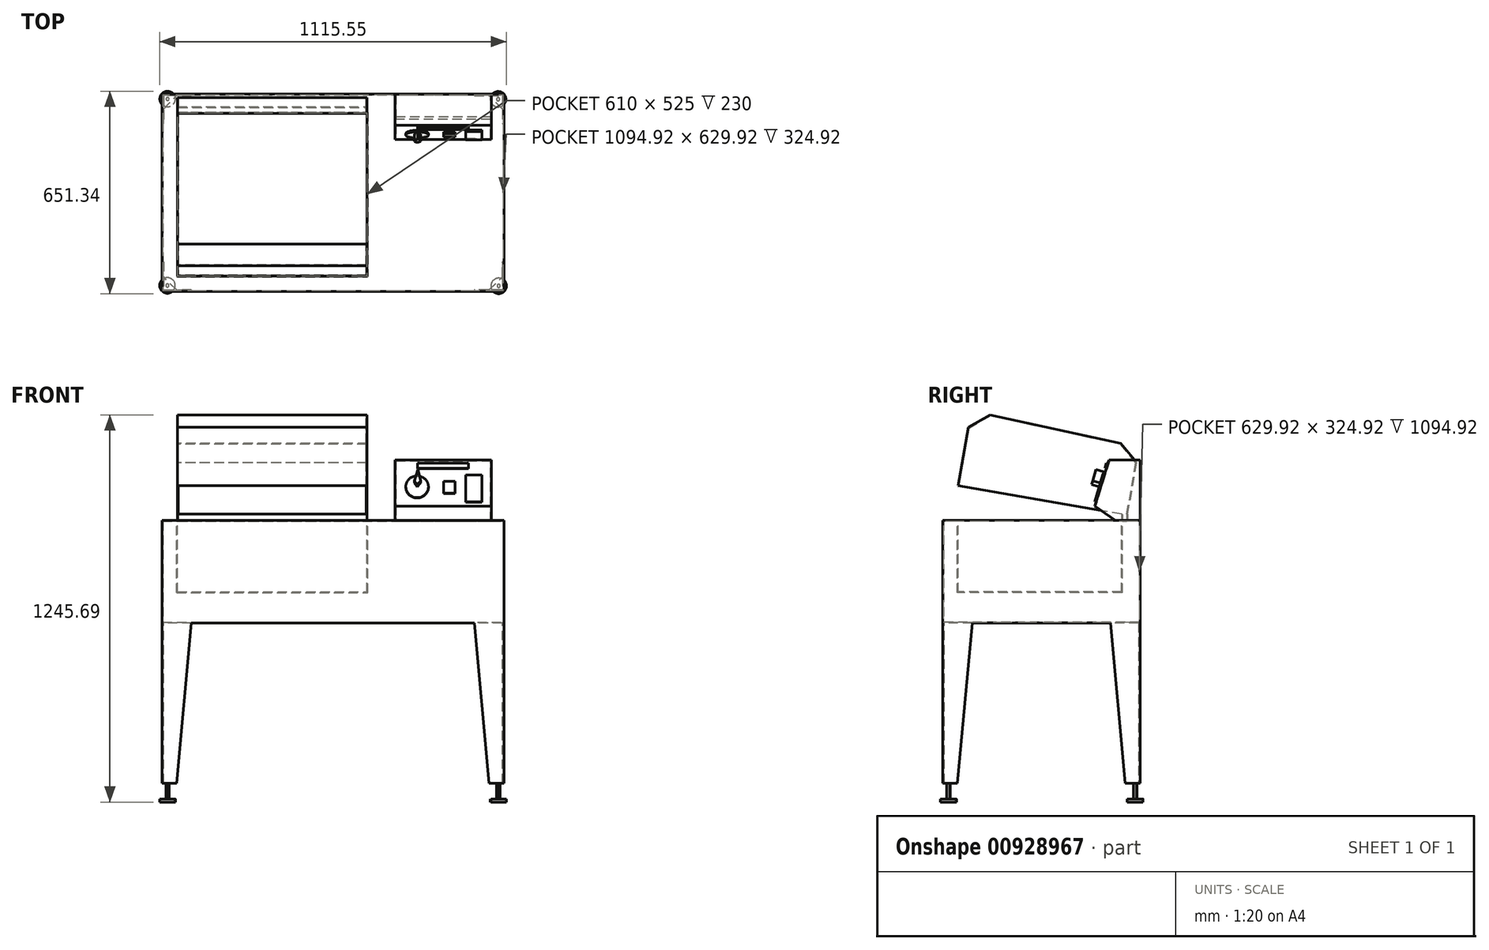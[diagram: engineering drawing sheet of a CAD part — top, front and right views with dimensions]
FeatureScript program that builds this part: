
annotation { "Feature Type Name" : "Feature", "Feature Type Description" : "" }
export const myFeature = defineFeature(function(context is Context, id is Id, definition is map)
    precondition{}
    {
        {
            var Q0;
            Q0=qCreatedBy(makeId("Front.planeOp"),FACE);
            var sketch = newSketch(context, id + "F0", { "sketchPlane" : qUnion([Q0])});
            skLineSegment(sketch, "E0", {"start": v(0, 749.43) * mm, "end": v(0, -565.58) * mm, "construction": true});
            skLineSegment(sketch, "E1", {"start": v(-789.94, 0) * mm, "end": v(708.92, 0) * mm, "construction": true});
            skLineSegment(sketch, "E2.bottom", {"start": v(-550, 165) * mm, "end": v(550, 165) * mm});
            skLineSegment(sketch, "E2.top", {"start": v(-550, -165) * mm, "end": v(550, -165) * mm});
            skLineSegment(sketch, "E2.left", {"start": v(-550, 165) * mm, "end": v(-550, -165) * mm});
            skLineSegment(sketch, "E2.right", {"start": v(550, 165) * mm, "end": v(550, -165) * mm});
            skSolve(sketch);
        }
        {
            var Q0;
            Q0 = qSketchRegion(id + "F0", true);
            extrude(context, id + "F1", {"entities" : qUnion([Q0]), "oppositeDirection" : true, "depth" : 635 * mm, "offsetDistance" : 25.4 * mm});
        }
        {
            var Q0;
            Q0=makeQuery(id+"F1.opExtrude","SWEPT_FACE",FACE,{"disambiguationData":[OSD([sQuery(id+"F0.wireOp",EDGE,"E2.bottom")])]});
            var sketch = newSketch(context, id + "F2", { "sketchPlane" : qUnion([Q0])});
            skLineSegment(sketch, "E3.bottom", {"start": v(510, 635) * mm, "end": v(200, 635) * mm});
            skLineSegment(sketch, "E3.top", {"start": v(510, 465) * mm, "end": v(200, 465) * mm});
            skLineSegment(sketch, "E3.left", {"start": v(510, 635) * mm, "end": v(510, 465) * mm});
            skLineSegment(sketch, "E3.right", {"start": v(200, 635) * mm, "end": v(200, 465) * mm});
            skSolve(sketch);
        }
        {
            var Q0;
            Q0 = qSketchRegion(id + "F2", true);
            extrude(context, id + "F3", {"entities" : qUnion([Q0]), "operationType" : NewBodyOperationType.ADD, "depth" : 195 * mm, "offsetDistance" : 25.4 * mm});
        }
        {
            var Q0;
            Q0=makeQuery(id+"F3.opExtrude","SWEPT_FACE",FACE,{"disambiguationData":[OSD([sQuery(id+"F2.wireOp",EDGE,"E3.left")])]});
            var sketch = newSketch(context, id + "F4", { "sketchPlane" : qUnion([Q0])});
            skLineSegment(sketch, "E4", {"start": v(635, 360) * mm, "end": v(535, 360) * mm});
            skLineSegment(sketch, "E5", {"start": v(635, 165) * mm, "end": v(555, 165) * mm});
            skLineSegment(sketch, "E6", {"start": v(555, 165) * mm, "end": v(489.35, 210.72) * mm});
            skLineSegment(sketch, "E7", {"start": v(489.35, 210.72) * mm, "end": v(535, 360) * mm});
            skLineSegment(sketch, "E8", {"start": v(555, 165) * mm, "end": v(465, 165) * mm});
            skLineSegment(sketch, "E9", {"start": v(465, 165) * mm, "end": v(465, 360) * mm});
            skLineSegment(sketch, "E10", {"start": v(465, 360) * mm, "end": v(535, 360) * mm});
            skSolve(sketch);
        }
        {
            var Q0;
            Q0=makeQuery(id+"F4.imprint","IMPRINT",FACE,{"disambiguationData":[TD([[makeQuery(id+"F4.imprint","IMPRINT",EDGE,{"derivedFrom":sQuery(id+"F4.wireOp",EDGE,"E6")}),1.0]])]});
            extrude(context, id + "F5", {"entities" : qUnion([Q0]), "operationType" : NewBodyOperationType.REMOVE, "endBound" : BoundingType.UP_TO_NEXT, "oppositeDirection" : true, "depth" : 25.4 * mm, "offsetDistance" : 25.4 * mm});
        }
        {
            var Q0;
            Q0=makeQuery(id+"F5.boolean.opBoolean","MERGE",FACE,{"derivedFrom":[makeQuery(id+"F1.opExtrude","SWEPT_FACE",FACE,{"disambiguationData":[OSD([sQuery(id+"F0.wireOp",EDGE,"E2.bottom")])]})],"fromTools":[makeQuery(id+"F5.opExtrude","SWEPT_FACE",FACE,{"disambiguationData":[OSD([sQuery(id+"F4.wireOp",EDGE,"E8")])]})]});
            var sketch = newSketch(context, id + "F6", { "sketchPlane" : qUnion([Q0])});
            skLineSegment(sketch, "E11.bottom", {"start": v(-500, 575) * mm, "end": v(110, 575) * mm});
            skLineSegment(sketch, "E11.top", {"start": v(-500, 50) * mm, "end": v(110, 50) * mm});
            skLineSegment(sketch, "E11.left", {"start": v(-500, 575) * mm, "end": v(-500, 50) * mm});
            skLineSegment(sketch, "E11.right", {"start": v(110, 575) * mm, "end": v(110, 50) * mm});
            skSolve(sketch);
        }
        {
            var Q0;
            Q0 = qSketchRegion(id + "F6", true);
            extrude(context, id + "F7", {"entities" : qUnion([Q0]), "operationType" : NewBodyOperationType.REMOVE, "oppositeDirection" : true, "depth" : 230 * mm, "offsetDistance" : 25.4 * mm});
        }
        {
            var Q0;
            Q0=makeQuery(id+"F5.boolean.opBoolean","MERGE",FACE,{"derivedFrom":[makeQuery(id+"F1.opExtrude","SWEPT_FACE",FACE,{"disambiguationData":[OSD([sQuery(id+"F0.wireOp",EDGE,"E2.bottom")])]})],"fromTools":[makeQuery(id+"F5.opExtrude","SWEPT_FACE",FACE,{"disambiguationData":[OSD([sQuery(id+"F4.wireOp",EDGE,"E8")])]})]});
            var sketch = newSketch(context, id + "F8", { "sketchPlane" : qUnion([Q0])});
            skLineSegment(sketch, "E12.bottom", {"start": v(-500, 575) * mm, "end": v(110, 575) * mm});
            skLineSegment(sketch, "E12.top", {"start": v(-500, 595) * mm, "end": v(110, 595) * mm});
            skLineSegment(sketch, "E12.left", {"start": v(-500, 575) * mm, "end": v(-500, 595) * mm});
            skLineSegment(sketch, "E12.right", {"start": v(110, 575) * mm, "end": v(110, 595) * mm});
            skSolve(sketch);
        }
        {
            var Q0;
            Q0 = qSketchRegion(id + "F8", true);
            extrude(context, id + "F9", {"entities" : qUnion([Q0]), "operationType" : NewBodyOperationType.ADD, "depth" : 20 * mm, "offsetDistance" : 25.4 * mm});
        }
        {
            var Q0;
            Q0=makeQuery(id+"F9.opExtrude","SWEPT_FACE",FACE,{"disambiguationData":[OSD([sQuery(id+"F8.wireOp",EDGE,"E12.left")])]});
            var sketch = newSketch(context, id + "F10", { "sketchPlane" : qUnion([Q0])});
            skLineSegment(sketch, "E13", {"start": v(-575, 185) * mm, "end": v(-50, 277.57) * mm});
            skLineSegment(sketch, "E14", {"start": v(-50, 277.57) * mm, "end": v(-83, 464.69) * mm});
            skLineSegment(sketch, "E15", {"start": v(-595, 185) * mm, "end": v(-624.3, 351.17) * mm});
            skLineSegment(sketch, "E16", {"start": v(-624.3, 351.17) * mm, "end": v(-572.88, 412.45) * mm});
            skLineSegment(sketch, "E17", {"start": v(-83, 464.69) * mm, "end": v(-152.28, 504.69) * mm});
            skLineSegment(sketch, "E18", {"start": v(-572.88, 412.45) * mm, "end": v(-152.28, 504.69) * mm});
            skLineSegment(sketch, "E19", {"start": v(-595, 185) * mm, "end": v(-575, 185) * mm});
            skSolve(sketch);
        }
        {
            var Q0;
            Q0 = qSketchRegion(id + "F10", true);
            var Q1;
            Q1=makeQuery(id+"F9.opExtrude","CAP_VERTEX",VERTEX,{"disambiguationData":[OSD([sQuery(id+"F6.wireOp",EDGE,"E11.right"),sQuery(id+"F8.wireOp",EDGE,"E12.bottom"),sQuery(id+"F8.wireOp",EDGE,"E12.right")])],"isStart":false});
            extrude(context, id + "F11", {"entities" : qUnion([Q0]), "operationType" : NewBodyOperationType.ADD, "endBound" : BoundingType.UP_TO_VERTEX, "oppositeDirection" : true, "depth" : 25.4 * mm, "endBoundEntityVertex" : qUnion([Q1]), "offsetDistance" : 25.4 * mm});
        }
        {
            var Q0;
            Q0=makeQuery(id+"F11.opExtrude","SWEPT_FACE",FACE,{"disambiguationData":[OSD([sQuery(id+"F10.wireOp",EDGE,"E13")])]});
            shell(context, id + "F12", {"entities" : qUnion([Q0]), "thickness" : 2.54 * mm});
        }
        {
            var Q0;
            Q0=makeQuery(id+"F1.opExtrude","SWEPT_FACE",FACE,{"disambiguationData":[OSD([sQuery(id+"F0.wireOp",EDGE,"E2.top")])]});
            var sketch = newSketch(context, id + "F13", { "sketchPlane" : qUnion([Q0])});
            skLineSegment(sketch, "E20", {"start": v(-455, 0) * mm, "end": v(-550, 0) * mm});
            skLineSegment(sketch, "E21", {"start": v(-550, 0) * mm, "end": v(-550, -95) * mm});
            skLineSegment(sketch, "E22", {"start": v(-550, -95) * mm, "end": v(-545, -95) * mm});
            skLineSegment(sketch, "E23", {"start": v(-545, -95) * mm, "end": v(-545, -5) * mm});
            skLineSegment(sketch, "E24", {"start": v(-545, -5) * mm, "end": v(-455, -5) * mm});
            skLineSegment(sketch, "E25", {"start": v(-455, -5) * mm, "end": v(-455, 0) * mm});
            skLineSegment(sketch, "E26", {"start": v(455, 0) * mm, "end": v(550, 0) * mm});
            skLineSegment(sketch, "E27", {"start": v(550, 0) * mm, "end": v(550, -95) * mm});
            skLineSegment(sketch, "E28", {"start": v(550, -95) * mm, "end": v(545, -95) * mm});
            skLineSegment(sketch, "E29", {"start": v(545, -95) * mm, "end": v(545, -5) * mm});
            skLineSegment(sketch, "E30", {"start": v(545, -5) * mm, "end": v(455, -5) * mm});
            skLineSegment(sketch, "E31", {"start": v(455, -5) * mm, "end": v(455, 0) * mm});
            skLineSegment(sketch, "E32", {"start": v(-550, -540) * mm, "end": v(-550, -635) * mm});
            skLineSegment(sketch, "E33", {"start": v(-550, -635) * mm, "end": v(-455, -635) * mm});
            skLineSegment(sketch, "E34", {"start": v(-455, -635) * mm, "end": v(-455, -630) * mm});
            skLineSegment(sketch, "E35", {"start": v(-455, -630) * mm, "end": v(-545, -630) * mm});
            skLineSegment(sketch, "E36", {"start": v(-545, -630) * mm, "end": v(-545, -540) * mm});
            skLineSegment(sketch, "E37", {"start": v(-545, -540) * mm, "end": v(-550, -540) * mm});
            skLineSegment(sketch, "E38", {"start": v(550, -540) * mm, "end": v(550, -635) * mm});
            skLineSegment(sketch, "E39", {"start": v(550, -635) * mm, "end": v(455, -635) * mm});
            skLineSegment(sketch, "E40", {"start": v(455, -635) * mm, "end": v(455, -630) * mm});
            skLineSegment(sketch, "E41", {"start": v(455, -630) * mm, "end": v(545, -630) * mm});
            skLineSegment(sketch, "E42", {"start": v(545, -630) * mm, "end": v(545, -540) * mm});
            skLineSegment(sketch, "E43", {"start": v(545, -540) * mm, "end": v(550, -540) * mm});
            skSolve(sketch);
        }
        {
            var Q0;
            Q0 = qSketchRegion(id + "F13", true);
            extrude(context, id + "F14", {"entities" : qUnion([Q0]), "operationType" : NewBodyOperationType.ADD, "depth" : 515 * mm, "offsetDistance" : 25.4 * mm});
        }
        {
            var Q0;
            Q0=makeQuery(id+"F14.boolean.opBoolean","MERGE",FACE,{"derivedFrom":[makeQuery(id+"F1.opExtrude","CAP_FACE",FACE,{"disambiguationData":[OSD([sQuery(id+"F0.wireOp",EDGE,"E2.bottom"),sQuery(id+"F0.wireOp",EDGE,"E2.top"),sQuery(id+"F0.wireOp",EDGE,"E2.left"),sQuery(id+"F0.wireOp",EDGE,"E2.right")])],"isStart":true}),makeQuery(id+"F14.opExtrude","SWEPT_FACE",FACE,{"disambiguationData":[OSD([sQuery(id+"F13.wireOp",EDGE,"E20")])]})]});
            var sketch = newSketch(context, id + "F15", { "sketchPlane" : qUnion([Q0])});
            skLineSegment(sketch, "E44", {"start": v(-455, -165) * mm, "end": v(-502.5, -680) * mm});
            skLineSegment(sketch, "E45", {"start": v(-502.5, -680) * mm, "end": v(-455, -680) * mm});
            skLineSegment(sketch, "E46", {"start": v(-455, -680) * mm, "end": v(-455, -165) * mm});
            skSolve(sketch);
        }
        {
            var Q0;
            Q0 = qSketchRegion(id + "F15", true);
            extrude(context, id + "F16", {"entities" : qUnion([Q0]), "operationType" : NewBodyOperationType.REMOVE, "oppositeDirection" : true, "depth" : 25.4 * mm, "offsetDistance" : 25.4 * mm});
        }
        {
            var Q0;
            Q0=makeQuery(id+"F14.boolean.opBoolean","MERGE",FACE,{"derivedFrom":[makeQuery(id+"F1.opExtrude","SWEPT_FACE",FACE,{"disambiguationData":[OSD([sQuery(id+"F0.wireOp",EDGE,"E2.left")])]}),makeQuery(id+"F14.opExtrude","SWEPT_FACE",FACE,{"disambiguationData":[OSD([sQuery(id+"F13.wireOp",EDGE,"E21")])]})]});
            var sketch = newSketch(context, id + "F17", { "sketchPlane" : qUnion([Q0])});
            skLineSegment(sketch, "E47", {"start": v(-95, -165) * mm, "end": v(-47.5, -680) * mm});
            skLineSegment(sketch, "E48", {"start": v(-47.5, -680) * mm, "end": v(-95, -680) * mm});
            skLineSegment(sketch, "E49", {"start": v(-95, -680) * mm, "end": v(-95, -165) * mm});
            skSolve(sketch);
        }
        {
            var Q0;
            Q0 = qSketchRegion(id + "F17", true);
            extrude(context, id + "F18", {"entities" : qUnion([Q0]), "operationType" : NewBodyOperationType.REMOVE, "oppositeDirection" : true, "depth" : 25.4 * mm, "offsetDistance" : 25.4 * mm});
        }
        {
            var Q0;
            Q0=makeQuery(id+"F14.boolean.opBoolean","MERGE",FACE,{"derivedFrom":[makeQuery(id+"F1.opExtrude","CAP_FACE",FACE,{"disambiguationData":[OSD([sQuery(id+"F0.wireOp",EDGE,"E2.bottom"),sQuery(id+"F0.wireOp",EDGE,"E2.top"),sQuery(id+"F0.wireOp",EDGE,"E2.left"),sQuery(id+"F0.wireOp",EDGE,"E2.right")])],"isStart":true}),makeQuery(id+"F14.opExtrude","SWEPT_FACE",FACE,{"disambiguationData":[OSD([sQuery(id+"F13.wireOp",EDGE,"E20")])]}),makeQuery(id+"F14.opExtrude","SWEPT_FACE",FACE,{"disambiguationData":[OSD([sQuery(id+"F13.wireOp",EDGE,"E26")])]})]});
            var sketch = newSketch(context, id + "F19", { "sketchPlane" : qUnion([Q0])});
            skLineSegment(sketch, "E50", {"start": v(455, -165) * mm, "end": v(502.5, -680) * mm});
            skLineSegment(sketch, "E51", {"start": v(502.5, -680) * mm, "end": v(455, -680) * mm});
            skLineSegment(sketch, "E52", {"start": v(455, -680) * mm, "end": v(455, -165) * mm});
            skSolve(sketch);
        }
        {
            var Q0;
            Q0 = qSketchRegion(id + "F19", true);
            extrude(context, id + "F20", {"entities" : qUnion([Q0]), "operationType" : NewBodyOperationType.REMOVE, "oppositeDirection" : true, "depth" : 840.74 * mm, "offsetDistance" : 25.4 * mm});
        }
        {
            var Q0;
            Q0=makeQuery(id+"F14.boolean.opBoolean","MERGE",FACE,{"derivedFrom":[makeQuery(id+"F1.opExtrude","SWEPT_FACE",FACE,{"disambiguationData":[OSD([sQuery(id+"F0.wireOp",EDGE,"E2.right")])]}),makeQuery(id+"F14.opExtrude","SWEPT_FACE",FACE,{"disambiguationData":[OSD([sQuery(id+"F13.wireOp",EDGE,"E27")])]}),makeQuery(id+"F14.opExtrude","SWEPT_FACE",FACE,{"disambiguationData":[OSD([sQuery(id+"F13.wireOp",EDGE,"E38")])]})]});
            var sketch = newSketch(context, id + "F21", { "sketchPlane" : qUnion([Q0])});
            skLineSegment(sketch, "E53", {"start": v(95, -165) * mm, "end": v(47.5, -680) * mm});
            skLineSegment(sketch, "E54", {"start": v(47.5, -680) * mm, "end": v(95, -680) * mm});
            skLineSegment(sketch, "E55", {"start": v(95, -680) * mm, "end": v(95, -165) * mm});
            skLineSegment(sketch, "E56", {"start": v(540, -165) * mm, "end": v(587.5, -680) * mm});
            skLineSegment(sketch, "E57", {"start": v(587.5, -680) * mm, "end": v(540, -680) * mm});
            skLineSegment(sketch, "E58", {"start": v(540, -680) * mm, "end": v(540, -165) * mm});
            skSolve(sketch);
        }
        {
            var Q0;
            Q0 = qSketchRegion(id + "F21", true);
            extrude(context, id + "F22", {"entities" : qUnion([Q0]), "operationType" : NewBodyOperationType.REMOVE, "oppositeDirection" : true, "depth" : 25.4 * mm, "offsetDistance" : 25.4 * mm});
        }
        {
            var Q0;
            Q0=makeQuery(id+"F14.boolean.opBoolean","MERGE",FACE,{"derivedFrom":[makeQuery(id+"F3.boolean.opBoolean","MERGE",FACE,{"derivedFrom":[makeQuery(id+"F1.opExtrude","CAP_FACE",FACE,{"disambiguationData":[OSD([sQuery(id+"F0.wireOp",EDGE,"E2.bottom"),sQuery(id+"F0.wireOp",EDGE,"E2.top"),sQuery(id+"F0.wireOp",EDGE,"E2.left"),sQuery(id+"F0.wireOp",EDGE,"E2.right")])],"isStart":false}),makeQuery(id+"F3.opExtrude","SWEPT_FACE",FACE,{"disambiguationData":[OSD([sQuery(id+"F2.wireOp",EDGE,"E3.bottom")])]})]}),makeQuery(id+"F14.opExtrude","SWEPT_FACE",FACE,{"disambiguationData":[OSD([sQuery(id+"F13.wireOp",EDGE,"E33")])]}),makeQuery(id+"F14.opExtrude","SWEPT_FACE",FACE,{"disambiguationData":[OSD([sQuery(id+"F13.wireOp",EDGE,"E39")])]})]});
            var sketch = newSketch(context, id + "F23", { "sketchPlane" : qUnion([Q0])});
            skLineSegment(sketch, "E59", {"start": v(455, -165) * mm, "end": v(502.5, -680) * mm});
            skLineSegment(sketch, "E60", {"start": v(502.5, -680) * mm, "end": v(455, -680) * mm});
            skLineSegment(sketch, "E61", {"start": v(455, -680) * mm, "end": v(455, -165) * mm});
            skSolve(sketch);
        }
        {
            var Q0;
            Q0 = qSketchRegion(id + "F23", true);
            extrude(context, id + "F24", {"entities" : qUnion([Q0]), "operationType" : NewBodyOperationType.REMOVE, "oppositeDirection" : true, "depth" : 25.4 * mm, "offsetDistance" : 25.4 * mm});
        }
        {
            var Q0;
            Q0=makeQuery(id+"F14.boolean.opBoolean","MERGE",FACE,{"derivedFrom":[makeQuery(id+"F1.opExtrude","SWEPT_FACE",FACE,{"disambiguationData":[OSD([sQuery(id+"F0.wireOp",EDGE,"E2.left")])]}),makeQuery(id+"F14.opExtrude","SWEPT_FACE",FACE,{"disambiguationData":[OSD([sQuery(id+"F13.wireOp",EDGE,"E21")])]}),makeQuery(id+"F14.opExtrude","SWEPT_FACE",FACE,{"disambiguationData":[OSD([sQuery(id+"F13.wireOp",EDGE,"E32")])]})]});
            var sketch = newSketch(context, id + "F25", { "sketchPlane" : qUnion([Q0])});
            skLineSegment(sketch, "E62", {"start": v(-540, -165) * mm, "end": v(-587.5, -680) * mm});
            skLineSegment(sketch, "E63", {"start": v(-587.5, -680) * mm, "end": v(-540, -680) * mm});
            skLineSegment(sketch, "E64", {"start": v(-540, -680) * mm, "end": v(-540, -165) * mm});
            skSolve(sketch);
        }
        {
            var Q0;
            Q0 = qSketchRegion(id + "F25", true);
            extrude(context, id + "F26", {"entities" : qUnion([Q0]), "operationType" : NewBodyOperationType.REMOVE, "oppositeDirection" : true, "depth" : 25.4 * mm, "offsetDistance" : 25.4 * mm});
        }
        {
            var Q0;
            Q0=makeQuery(id+"F5.boolean.opBoolean","COPY",FACE,{"derivedFrom":makeQuery(id+"F5.opExtrude","SWEPT_FACE",FACE,{"disambiguationData":[OSD([sQuery(id+"F4.wireOp",EDGE,"E7")])]})});
            var sketch = newSketch(context, id + "F27", { "sketchPlane" : qUnion([Q0])});
            skCircle(sketch, "E65", {"center": v(270.73, 408.7) * mm, "radius": 36.44 * mm});
            skLineSegment(sketch, "E66.bottom", {"start": v(272.44, 488.09) * mm, "end": v(435.25, 488.09) * mm});
            skLineSegment(sketch, "E66.top", {"start": v(272.44, 471.45) * mm, "end": v(435.25, 471.45) * mm});
            skLineSegment(sketch, "E66.left", {"start": v(272.44, 488.09) * mm, "end": v(272.44, 471.45) * mm});
            skLineSegment(sketch, "E66.right", {"start": v(435.25, 488.09) * mm, "end": v(435.25, 471.45) * mm});
            skLineSegment(sketch, "E67.bottom", {"start": v(356.47, 427.63) * mm, "end": v(392.9, 427.63) * mm});
            skLineSegment(sketch, "E67.top", {"start": v(356.47, 387.14) * mm, "end": v(392.9, 387.14) * mm});
            skLineSegment(sketch, "E67.left", {"start": v(356.47, 427.63) * mm, "end": v(356.47, 387.14) * mm});
            skLineSegment(sketch, "E67.right", {"start": v(392.9, 427.63) * mm, "end": v(392.9, 387.14) * mm});
            skLineSegment(sketch, "E68.bottom", {"start": v(427.5, 448.7) * mm, "end": v(478.96, 448.7) * mm});
            skLineSegment(sketch, "E68.top", {"start": v(427.5, 358.45) * mm, "end": v(478.96, 358.45) * mm});
            skLineSegment(sketch, "E68.left", {"start": v(427.5, 448.7) * mm, "end": v(427.5, 358.45) * mm});
            skLineSegment(sketch, "E68.right", {"start": v(478.96, 448.7) * mm, "end": v(478.96, 358.45) * mm});
            skSolve(sketch);
        }
        {
            var Q0;
            Q0 = qSketchRegion(id + "F27", true);
            extrude(context, id + "F28", {"entities" : qUnion([Q0]), "operationType" : NewBodyOperationType.ADD, "depth" : 5 * mm, "offsetDistance" : 25.4 * mm});
        }
        {
            var Q0;
            Q0=makeQuery(id+"F28.opExtrude","CAP_FACE",FACE,{"disambiguationData":[OSD([sQuery(id+"F27.wireOp",EDGE,"E65")])],"isStart":false});
            var sketch = newSketch(context, id + "F29", { "sketchPlane" : qUnion([Q0])});
            skLineSegment(sketch, "E69", {"start": v(270.73, 408.7) * mm, "end": v(261.6, 421.16) * mm});
            skLineSegment(sketch, "E70", {"start": v(261.6, 421.16) * mm, "end": v(274.02, 458.55) * mm});
            skLineSegment(sketch, "E71", {"start": v(274.02, 458.55) * mm, "end": v(282.52, 421.16) * mm});
            skLineSegment(sketch, "E72", {"start": v(282.52, 421.16) * mm, "end": v(270.73, 408.7) * mm});
            skSolve(sketch);
        }
        {
            var Q0;
            Q0 = qSketchRegion(id + "F29", true);
            extrude(context, id + "F30", {"entities" : qUnion([Q0]), "operationType" : NewBodyOperationType.ADD, "depth" : 25.4 * mm, "offsetDistance" : 25.4 * mm});
        }
        {
            var Q0;
            Q0=makeQuery(id+"F14.opExtrude","CAP_FACE",FACE,{"disambiguationData":[OSD([sQuery(id+"F13.wireOp",EDGE,"E20"),sQuery(id+"F13.wireOp",EDGE,"E21"),sQuery(id+"F13.wireOp",EDGE,"E22"),sQuery(id+"F13.wireOp",EDGE,"E23"),sQuery(id+"F13.wireOp",EDGE,"E24"),sQuery(id+"F13.wireOp",EDGE,"E25")])],"isStart":false});
            var sketch = newSketch(context, id + "F31", { "sketchPlane" : qUnion([Q0])});
            skLineSegment(sketch, "E73", {"start": v(-502.5, -5) * mm, "end": v(-545, -47.5) * mm});
            skLineSegment(sketch, "E74", {"start": v(-545, -47.5) * mm, "end": v(-545, -5) * mm});
            skLineSegment(sketch, "E75", {"start": v(-545, -5) * mm, "end": v(-502.5, -5) * mm});
            skLineSegment(sketch, "E76", {"start": v(-545, -587.5) * mm, "end": v(-502.5, -630) * mm});
            skLineSegment(sketch, "E77", {"start": v(-502.5, -630) * mm, "end": v(-545, -630) * mm});
            skLineSegment(sketch, "E78", {"start": v(-545, -630) * mm, "end": v(-545, -587.5) * mm});
            skLineSegment(sketch, "E79", {"start": v(545, -587.5) * mm, "end": v(502.5, -630) * mm});
            skLineSegment(sketch, "E80", {"start": v(502.5, -630) * mm, "end": v(545, -630) * mm});
            skLineSegment(sketch, "E81", {"start": v(545, -630) * mm, "end": v(545, -587.5) * mm});
            skLineSegment(sketch, "E82", {"start": v(545, -5) * mm, "end": v(502.5, -5) * mm});
            skLineSegment(sketch, "E83", {"start": v(502.5, -5) * mm, "end": v(545, -47.5) * mm});
            skLineSegment(sketch, "E84", {"start": v(545, -47.5) * mm, "end": v(545, -5) * mm});
            skSolve(sketch);
        }
        {
            var Q0;
            Q0 = qSketchRegion(id + "F31", true);
            extrude(context, id + "F32", {"entities" : qUnion([Q0]), "operationType" : NewBodyOperationType.ADD, "depth" : 1 * mm, "offsetDistance" : 25.4 * mm});
        }
        {
            var Q0;
            Q0=makeQuery(id+"F32.opExtrude","CAP_FACE",FACE,{"disambiguationData":[OSD([sQuery(id+"F31.wireOp",EDGE,"E73"),sQuery(id+"F31.wireOp",EDGE,"E74"),sQuery(id+"F31.wireOp",EDGE,"E75")])],"isStart":false});
            var sketch = newSketch(context, id + "F33", { "sketchPlane" : qUnion([Q0])});
            skCircle(sketch, "E85", {"center": v(-532.45, -19.55) * mm, "radius": 5 * mm});
            skCircle(sketch, "E86", {"center": v(-531.86, -619.5) * mm, "radius": 5 * mm});
            skCircle(sketch, "E87", {"center": v(533.1, -18.17) * mm, "radius": 5 * mm});
            skCircle(sketch, "E88", {"center": v(531.24, -618.72) * mm, "radius": 5 * mm});
            skSolve(sketch);
        }
        {
            var Q0;
            Q0 = qSketchRegion(id + "F33", true);
            extrude(context, id + "F34", {"entities" : qUnion([Q0]), "depth" : 50 * mm, "offsetDistance" : 25.4 * mm});
        }
        {
            var Q0;
            Q0=makeQuery(id+"F34.opExtrude","CAP_FACE",FACE,{"disambiguationData":[OSD([sQuery(id+"F33.wireOp",EDGE,"E86")])],"isStart":false});
            var sketch = newSketch(context, id + "F35", { "sketchPlane" : qUnion([Q0])});
            skCircle(sketch, "E89", {"center": v(-531.86, -619.5) * mm, "radius": 25 * mm});
            skCircle(sketch, "E90", {"center": v(531.24, -618.72) * mm, "radius": 25 * mm});
            skCircle(sketch, "E91", {"center": v(533.1, -18.17) * mm, "radius": 25 * mm});
            skCircle(sketch, "E92", {"center": v(-532.45, -19.55) * mm, "radius": 25 * mm});
            skSolve(sketch);
        }
        {
            var Q0;
            Q0 = qSketchRegion(id + "F35", true);
            extrude(context, id + "F36", {"entities" : qUnion([Q0]), "depth" : 10 * mm, "offsetDistance" : 25.4 * mm});
        }
    });
